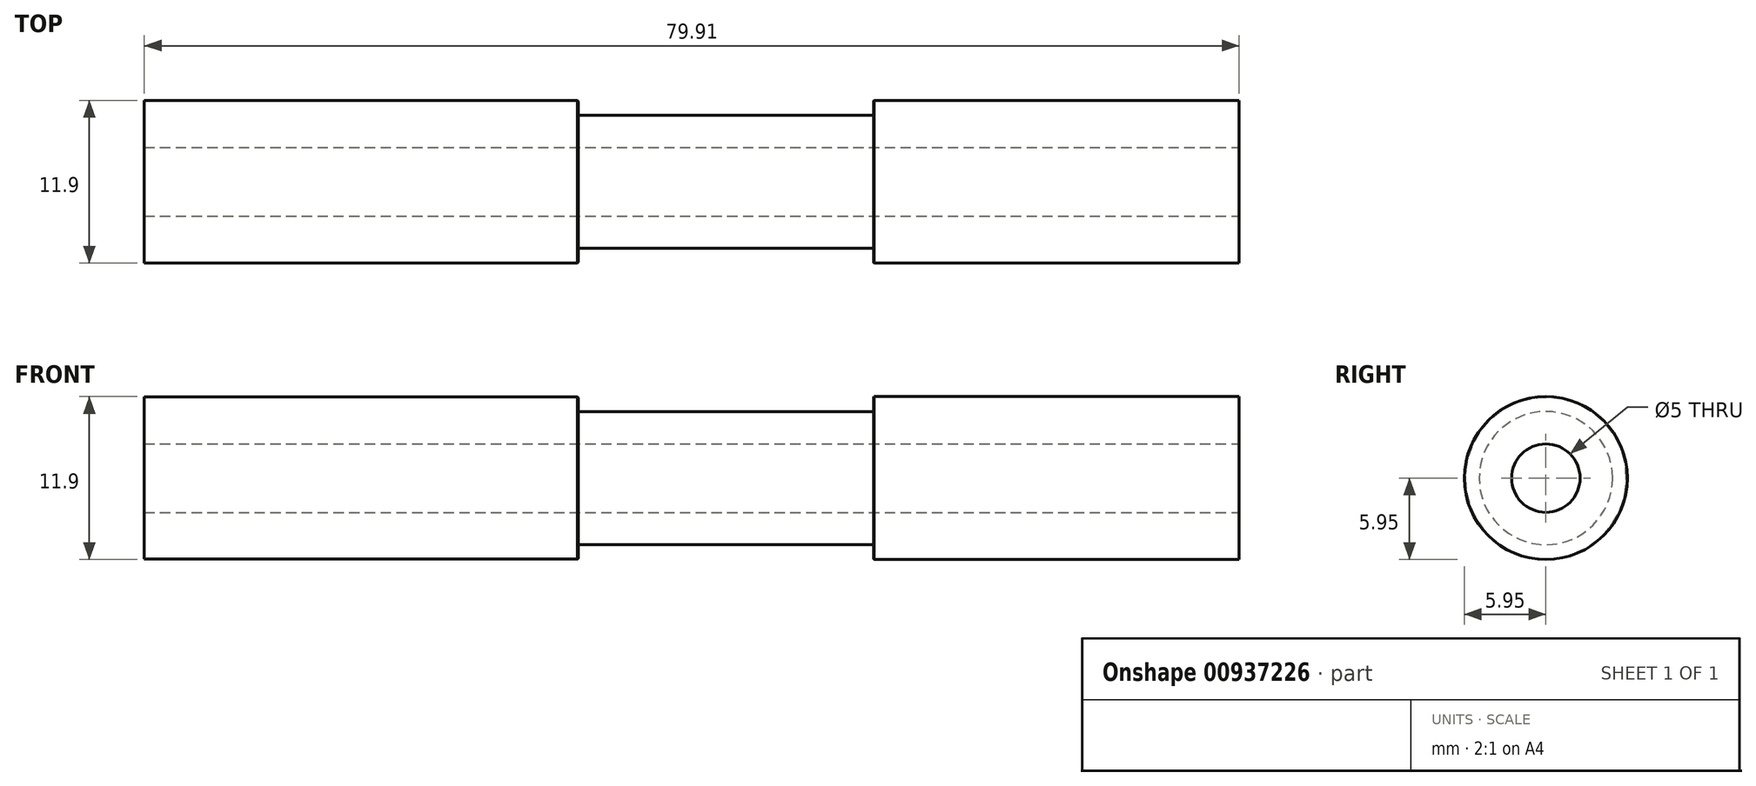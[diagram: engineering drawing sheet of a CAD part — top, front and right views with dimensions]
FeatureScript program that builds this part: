
annotation { "Feature Type Name" : "Feature", "Feature Type Description" : "" }
export const myFeature = defineFeature(function(context is Context, id is Id, definition is map)
    precondition{}
    {
        {
            var Q0;
            Q0=qCreatedBy(makeId("Right.planeOp"),FACE);
            var sketch = newSketch(context, id + "F0", { "sketchPlane" : qUnion([Q0])});
            skCircle(sketch, "E0", {"center": v(0, 0) * mm, "radius": 5.92 * mm});
            skSolve(sketch);
        }
        {
            var Q0;
            Q0=makeQuery(id+"F0.imprint","IMPRINT",FACE,{"disambiguationData":[TD([[makeQuery(id+"F0.imprint","IMPRINT",EDGE,{"derivedFrom":sQuery(id+"F0.wireOp",EDGE,"E0")}),1.0]])]});
            var Q1;
            Q1=sQuery(id+"F0.wireOp",EDGE,"E0");
            extrude(context, id + "F1", {"entities" : qUnion([Q0]), "surfaceEntities" : qUnion([Q1]), "depth" : 31.68 * mm, "offsetDistance" : 25 * mm});
        }
        {
            var Q0;
            Q0=makeQuery(id+"F1.opExtrude","CAP_FACE",FACE,{"disambiguationData":[OSD([sQuery(id+"F0.wireOp",EDGE,"E0")])],"isStart":false});
            var sketch = newSketch(context, id + "F2", { "sketchPlane" : qUnion([Q0])});
            skCircle(sketch, "E1", {"center": v(0, 0) * mm, "radius": 4.87 * mm});
            skSolve(sketch);
        }
        {
            var Q0;
            Q0 = qSketchRegion(id + "F2", true);
            extrude(context, id + "F3", {"entities" : qUnion([Q0]), "operationType" : NewBodyOperationType.ADD, "depth" : 21.55 * mm, "offsetDistance" : 25 * mm});
        }
        {
            var Q0;
            Q0=makeQuery(id+"F3.opExtrude","CAP_FACE",FACE,{"disambiguationData":[OSD([sQuery(id+"F2.wireOp",EDGE,"E1")])],"isStart":false});
            var sketch = newSketch(context, id + "F4", { "sketchPlane" : qUnion([Q0])});
            skCircle(sketch, "E2", {"center": v(0, 0) * mm, "radius": 5.95 * mm});
            skSolve(sketch);
        }
        {
            var Q0;
            Q0=makeQuery(id+"F4.imprint","IMPRINT",FACE,{"disambiguationData":[TD([[makeQuery(id+"F4.imprint","IMPRINT",EDGE,{"derivedFrom":sQuery(id+"F4.wireOp",EDGE,"E2")}),1.0]])]});
            var Q1;
            Q1=makeQuery(id+"F4.imprint","IMPRINT",FACE,{"disambiguationData":[TD([[makeQuery(id+"F4.imprint","IMPRINT",EDGE,{"derivedFrom":makeQuery(id+"F3.opExtrude","CAP_EDGE",EDGE,{"disambiguationData":[OSD([sQuery(id+"F2.wireOp",EDGE,"E1")])],"isStart":false})}),1.0]])]});
            var Q2;
            Q2=sQuery(id+"F4.wireOp",EDGE,"E2");
            extrude(context, id + "F5", {"entities" : qUnion([Q0, Q1]), "operationType" : NewBodyOperationType.ADD, "surfaceEntities" : qUnion([Q2]), "depth" : 26.68 * mm, "offsetDistance" : 25 * mm});
        }
        {
            var Q0;
            Q0=makeQuery(id+"F5.opExtrude","CAP_FACE",FACE,{"disambiguationData":[OSD([sQuery(id+"F4.wireOp",EDGE,"E2")])],"isStart":false});
            var sketch = newSketch(context, id + "F6", { "sketchPlane" : qUnion([Q0])});
            skCircle(sketch, "E3", {"center": v(0, 0) * mm, "radius": 2.13 * mm});
            skSolve(sketch);
        }
        {
            var Q0;
            Q0=sQuery(id+"F6.wireOp",VERTEX,"E3.center");
            var Q1;
            Q1=makeQuery(id+"F1.opExtrude","SWEPT_BODY",BODY,{"disambiguationData":[OSD([sQuery(id+"F0.wireOp",EDGE,"E0")])]});
            hole(context, id + "F7", {"style" : HoleStyle.SIMPLE, "endStyle" : HoleEndStyle.THROUGH, "holeDiameter" : 5 * mm, "majorDiameter" : 5 * mm, "isTappedThrough" : true, "tappedDepth" : 12 * mm, "tapClearance" : 3, "locations" : qUnion([Q0]), "scope" : qUnion([Q1])});
        }
        {
            var Q0;
            Q0=makeQuery(id+"F1.opExtrude","CAP_EDGE",EDGE,{"disambiguationData":[OSD([sQuery(id+"F0.wireOp",EDGE,"E0")])],"isStart":false});
            chamfer(context, id + "F8", {"entities" : qUnion([Q0]), "width" : 0.05 * mm, "tangentPropagation" : true});
        }
        {
            var Q0;
            Q0=makeQuery(id+"F5.opExtrude","CAP_EDGE",EDGE,{"disambiguationData":[OSD([sQuery(id+"F4.wireOp",EDGE,"E2")])],"isStart":true});
            chamfer(context, id + "F9", {"entities" : qUnion([Q0]), "width" : 0.05 * mm, "tangentPropagation" : true});
        }
    });
